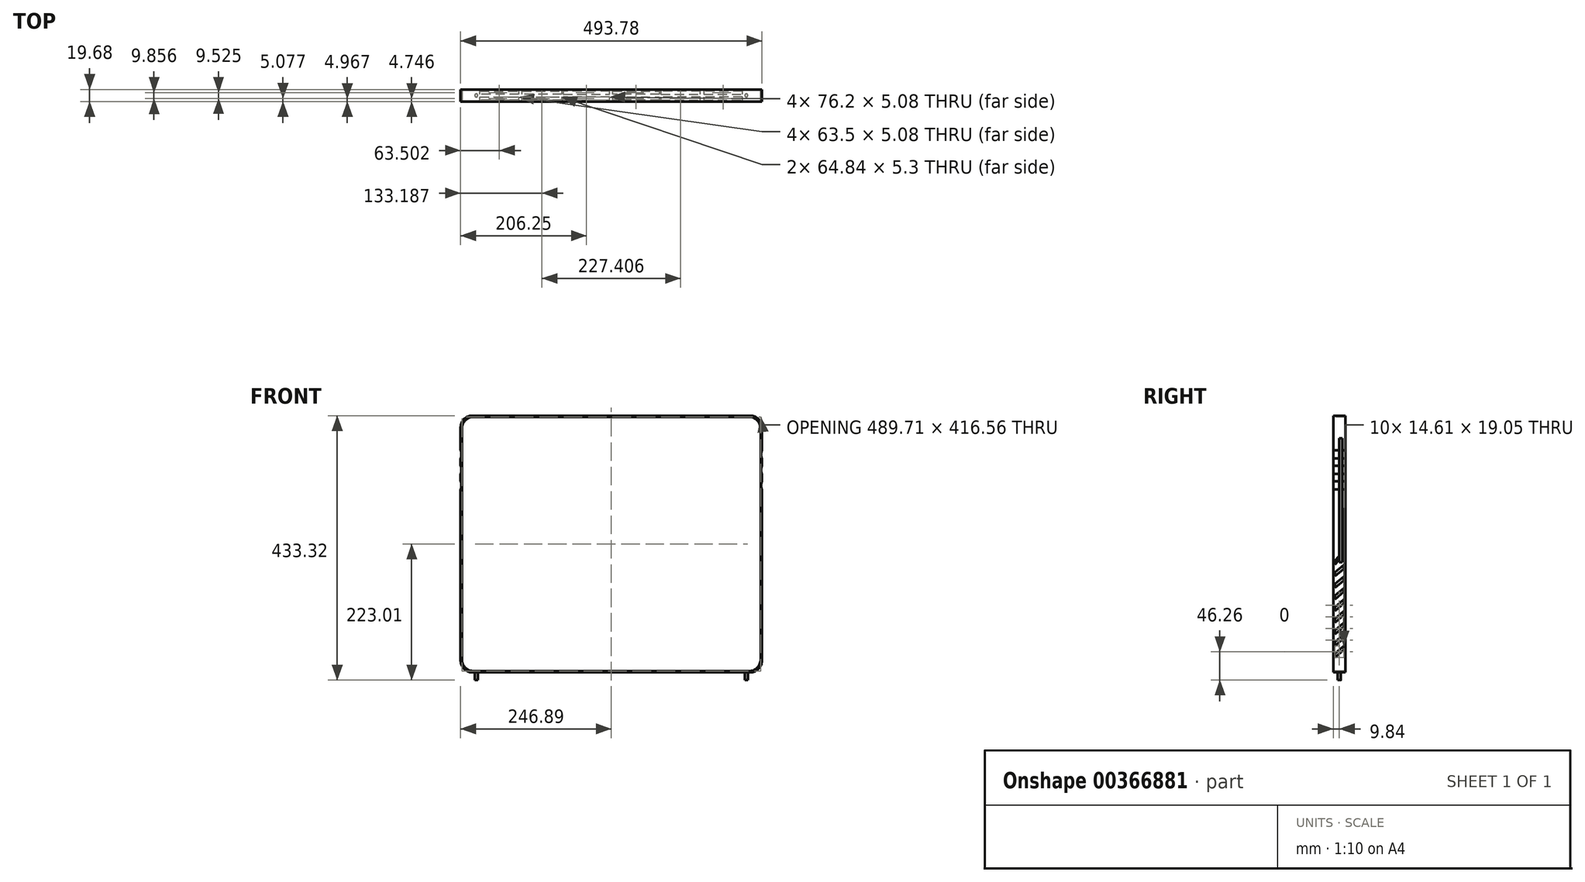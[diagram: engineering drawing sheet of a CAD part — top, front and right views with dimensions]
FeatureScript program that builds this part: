
annotation { "Feature Type Name" : "Feature", "Feature Type Description" : "" }
export const myFeature = defineFeature(function(context is Context, id is Id, definition is map)
    precondition{}
    {
        {
            var Q0;
            Q0=qCreatedBy(makeId("Front.planeOp"),FACE);
            var sketch = newSketch(context, id + "F0", { "sketchPlane" : qUnion([Q0])});
            skLineSegment(sketch, "E0.bottom", {"start": v(246.89, 210.31) * mm, "end": v(-246.89, 210.31) * mm});
            skLineSegment(sketch, "E0.top", {"start": v(246.89, -210.31) * mm, "end": v(-246.89, -210.31) * mm});
            skLineSegment(sketch, "E0.left", {"start": v(246.89, 210.31) * mm, "end": v(246.89, -210.31) * mm});
            skLineSegment(sketch, "E0.right", {"start": v(-246.89, 210.31) * mm, "end": v(-246.89, -210.31) * mm});
            skPoint(sketch, "E0.middle", {"position": v(0, 0) * mm});
            skSolve(sketch);
        }
        {
            var Q0;
            Q0 = qSketchRegion(id + "F0", true);
            extrude(context, id + "F1", {"entities" : qUnion([Q0]), "endBound" : BoundingType.SYMMETRIC, "oppositeDirection" : true, "depth" : 19.68 * mm});
        }
        {
            var Q0;
            Q0=makeQuery(id+"F1.opExtrude","SWEPT_EDGE",EDGE,{"disambiguationData":[OSD([sQuery(id+"F0.wireOp",EDGE,"E0.bottom"),sQuery(id+"F0.wireOp",EDGE,"E0.left")])]});
            fillet(context, id + "F2", {"entities" : qUnion([Q0]), "radius" : 19.05 * mm, "tangentPropagation" : true, "allowEdgeOverflow" : false});
        }
        {
            var Q0;
            Q0=makeQuery(id+"F1.opExtrude","SWEPT_EDGE",EDGE,{"disambiguationData":[OSD([sQuery(id+"F0.wireOp",EDGE,"E0.bottom"),sQuery(id+"F0.wireOp",EDGE,"E0.right")])]});
            fillet(context, id + "F3", {"entities" : qUnion([Q0]), "radius" : 19.05 * mm, "tangentPropagation" : true, "allowEdgeOverflow" : false});
        }
        {
            var Q0;
            Q0=makeQuery(id+"F1.opExtrude","SWEPT_EDGE",EDGE,{"disambiguationData":[OSD([sQuery(id+"F0.wireOp",EDGE,"E0.top"),sQuery(id+"F0.wireOp",EDGE,"E0.left")])]});
            fillet(context, id + "F4", {"entities" : qUnion([Q0]), "radius" : 19.05 * mm, "tangentPropagation" : true, "allowEdgeOverflow" : false});
        }
        {
            var Q0;
            Q0=makeQuery(id+"F1.opExtrude","SWEPT_EDGE",EDGE,{"disambiguationData":[OSD([sQuery(id+"F0.wireOp",EDGE,"E0.top"),sQuery(id+"F0.wireOp",EDGE,"E0.right")])]});
            fillet(context, id + "F5", {"entities" : qUnion([Q0]), "radius" : 19.05 * mm, "tangentPropagation" : true, "allowEdgeOverflow" : false});
        }
        {
            var Q0;
            Q0=qCreatedBy(makeId("Front.planeOp"),FACE);
            var sketch = newSketch(context, id + "F6", { "sketchPlane" : qUnion([Q0])});
            skLineSegment(sketch, "E1.bottom", {"start": v(225.8, 208.28) * mm, "end": v(-225.8, 208.28) * mm});
            skLineSegment(sketch, "E1.top", {"start": v(225.8, -208.28) * mm, "end": v(-225.8, -208.28) * mm});
            skLineSegment(sketch, "E1.left", {"start": v(244.86, 189.23) * mm, "end": v(244.86, -189.23) * mm});
            skLineSegment(sketch, "E1.right", {"start": v(-244.86, 189.23) * mm, "end": v(-244.86, -189.23) * mm});
            skPoint(sketch, "E1.middle", {"position": v(0, 0) * mm});
            skPoint(sketch, "E2.visualSharp", {"position": v(-244.86, 208.28) * mm});
            skArc(sketch, "E2.filletArc", {"start": v(-225.8, 208.28) * mm, "mid": v(-239.28, 202.7) * mm, "end": v(-244.86, 189.23) * mm});
            skPoint(sketch, "E3.visualSharp", {"position": v(244.86, 208.28) * mm});
            skArc(sketch, "E3.filletArc", {"start": v(244.86, 189.23) * mm, "mid": v(239.28, 202.7) * mm, "end": v(225.8, 208.28) * mm});
            skPoint(sketch, "E4.visualSharp", {"position": v(-244.86, -208.28) * mm});
            skArc(sketch, "E4.filletArc", {"start": v(-244.86, -189.23) * mm, "mid": v(-239.28, -202.7) * mm, "end": v(-225.8, -208.28) * mm});
            skPoint(sketch, "E5.visualSharp", {"position": v(244.86, -208.28) * mm});
            skArc(sketch, "E5.filletArc", {"start": v(225.8, -208.28) * mm, "mid": v(239.28, -202.7) * mm, "end": v(244.86, -189.23) * mm});
            skSolve(sketch);
        }
        {
            var Q0;
            Q0 = qSketchRegion(id + "F6", true);
            var Q1;
            Q1=sQuery(id+"F6.wireOp",EDGE,"E2.filletArc");
            var Q2;
            Q2=sQuery(id+"F6.wireOp",EDGE,"E1.bottom");
            var Q3;
            Q3=sQuery(id+"F6.wireOp",EDGE,"E3.filletArc");
            var Q4;
            Q4=sQuery(id+"F6.wireOp",EDGE,"E1.left");
            var Q5;
            Q5=sQuery(id+"F6.wireOp",EDGE,"E5.filletArc");
            var Q6;
            Q6=sQuery(id+"F6.wireOp",EDGE,"E1.top");
            var Q7;
            Q7=sQuery(id+"F6.wireOp",EDGE,"E4.filletArc");
            var Q8;
            Q8=sQuery(id+"F6.wireOp",EDGE,"E1.right");
            extrude(context, id + "F7", {"entities" : qUnion([Q0]), "operationType" : NewBodyOperationType.REMOVE, "surfaceEntities" : qUnion([Q1, Q2, Q3, Q4, Q5, Q6, Q7, Q8]), "endBound" : BoundingType.THROUGH_ALL, "oppositeDirection" : true, "depth" : 25.4 * mm});
        }
        {
            var Q0;
            Q0 = qSketchRegion(id + "F6", true);
            extrude(context, id + "F8", {"entities" : qUnion([Q0]), "operationType" : NewBodyOperationType.REMOVE, "oppositeDirection" : true, "depth" : 50.8 * mm});
        }
        {
            var Q0;
            Q0 = qSketchRegion(id + "F6", true);
            extrude(context, id + "F9", {"entities" : qUnion([Q0]), "operationType" : NewBodyOperationType.REMOVE, "endBound" : BoundingType.THROUGH_ALL, "depth" : 76.2 * mm});
        }
        {
            var Q0;
            Q0=qCreatedBy(makeId("Right.planeOp"),FACE);
            var sketch = newSketch(context, id + "F10", { "sketchPlane" : qUnion([Q0])});
            skLineSegment(sketch, "E6", {"start": v(7.3, -34.52) * mm, "end": v(7.3, -40.87) * mm});
            skLineSegment(sketch, "E7", {"start": v(7.3, -53.57) * mm, "end": v(7.3, -59.92) * mm});
            skLineSegment(sketch, "E8", {"start": v(-7.3, -46.58) * mm, "end": v(-7.3, -52.92) * mm});
            skLineSegment(sketch, "E9", {"start": v(-7.3, -52.92) * mm, "end": v(7.3, -40.87) * mm});
            skLineSegment(sketch, "E10", {"start": v(7.3, -34.52) * mm, "end": v(-7.3, -46.58) * mm});
            skLineSegment(sketch, "E11", {"start": v(-7.3, -65.62) * mm, "end": v(-7.3, -71.97) * mm});
            skLineSegment(sketch, "E12", {"start": v(-7.3, -65.62) * mm, "end": v(7.3, -53.57) * mm});
            skLineSegment(sketch, "E13", {"start": v(7.3, -59.92) * mm, "end": v(-7.3, -71.97) * mm});
            skLineSegment(sketch, "E14", {"start": v(-7.3, -33.88) * mm, "end": v(-7.3, -27.54) * mm});
            skLineSegment(sketch, "E15", {"start": v(-7.3, -33.88) * mm, "end": v(-1.32, -27.53) * mm});
            skLineSegment(sketch, "E16", {"start": v(-1.32, -27.53) * mm, "end": v(-1.32, -21.17) * mm});
            skLineSegment(sketch, "E17", {"start": v(-7.3, -27.54) * mm, "end": v(-1.32, -21.17) * mm});
            skLineSegment(sketch, "E18", {"start": v(-7.3, -84.67) * mm, "end": v(-7.3, -91.02) * mm});
            skLineSegment(sketch, "E19", {"start": v(7.3, -72.62) * mm, "end": v(7.3, -78.32) * mm});
            skLineSegment(sketch, "E20", {"start": v(-7.3, -84.67) * mm, "end": v(7.3, -72.62) * mm});
            skLineSegment(sketch, "E21", {"start": v(7.3, -78.32) * mm, "end": v(-7.3, -91.02) * mm});
            skLineSegment(sketch, "E22", {"start": v(-7.3, -103.72) * mm, "end": v(-7.3, -110.07) * mm});
            skLineSegment(sketch, "E23", {"start": v(7.3, -97.37) * mm, "end": v(7.3, -91.02) * mm});
            skLineSegment(sketch, "E24", {"start": v(-7.3, -103.72) * mm, "end": v(7.3, -91.02) * mm});
            skLineSegment(sketch, "E25", {"start": v(7.3, -97.37) * mm, "end": v(-7.3, -110.07) * mm});
            skLineSegment(sketch, "E26", {"start": v(-7.3, -122.77) * mm, "end": v(-7.3, -129.12) * mm});
            skLineSegment(sketch, "E27", {"start": v(-7.3, -129.12) * mm, "end": v(7.3, -116.42) * mm});
            skLineSegment(sketch, "E28", {"start": v(7.3, -116.42) * mm, "end": v(7.3, -110.07) * mm});
            skLineSegment(sketch, "E29", {"start": v(7.3, -110.07) * mm, "end": v(-7.3, -122.77) * mm});
            skLineSegment(sketch, "E30", {"start": v(-7.3, -141.82) * mm, "end": v(-7.3, -148.17) * mm});
            skLineSegment(sketch, "E31", {"start": v(-7.3, -148.17) * mm, "end": v(7.3, -135.47) * mm});
            skLineSegment(sketch, "E32", {"start": v(7.3, -135.47) * mm, "end": v(7.3, -129.12) * mm});
            skLineSegment(sketch, "E33", {"start": v(7.3, -129.12) * mm, "end": v(-7.3, -141.82) * mm});
            skLineSegment(sketch, "E34", {"start": v(-7.3, -160.87) * mm, "end": v(-7.3, -167.22) * mm});
            skLineSegment(sketch, "E35", {"start": v(-7.3, -167.22) * mm, "end": v(7.3, -154.52) * mm});
            skLineSegment(sketch, "E36", {"start": v(7.3, -154.52) * mm, "end": v(7.3, -148.17) * mm});
            skLineSegment(sketch, "E37", {"start": v(7.3, -148.17) * mm, "end": v(-7.3, -160.87) * mm});
            skLineSegment(sketch, "E38", {"start": v(-7.3, -179.92) * mm, "end": v(-7.3, -186.27) * mm});
            skLineSegment(sketch, "E39", {"start": v(-7.3, -186.27) * mm, "end": v(7.3, -173.57) * mm});
            skLineSegment(sketch, "E40", {"start": v(7.3, -173.57) * mm, "end": v(7.3, -167.22) * mm});
            skLineSegment(sketch, "E41", {"start": v(7.3, -167.22) * mm, "end": v(-7.3, -179.92) * mm});
            skSolve(sketch);
        }
        {
            var Q0;
            Q0 = qSketchRegion(id + "F10", true);
            extrude(context, id + "F11", {"entities" : qUnion([Q0]), "operationType" : NewBodyOperationType.REMOVE, "oppositeDirection" : true, "depth" : 381 * mm});
        }
        {
            var Q0;
            Q0 = qSketchRegion(id + "F10", true);
            extrude(context, id + "F12", {"entities" : qUnion([Q0]), "operationType" : NewBodyOperationType.REMOVE, "depth" : 381 * mm});
        }
        {
            var Q0;
            Q0=qCreatedBy(makeId("Top.planeOp"),FACE);
            var sketch = newSketch(context, id + "F13", { "sketchPlane" : qUnion([Q0])});
            skLineSegment(sketch, "E42", {"start": v(-2.54, -7.3) * mm, "end": v(-2.54, -2.22) * mm});
            skLineSegment(sketch, "E43", {"start": v(-2.54, -2.22) * mm, "end": v(-78.74, -2.22) * mm});
            skLineSegment(sketch, "E44", {"start": v(-78.74, -2.22) * mm, "end": v(-78.74, -7.3) * mm});
            skLineSegment(sketch, "E45", {"start": v(-78.74, -7.3) * mm, "end": v(-2.54, -7.3) * mm});
            skLineSegment(sketch, "E46", {"start": v(-78.74, 2.22) * mm, "end": v(-2.54, 2.22) * mm});
            skLineSegment(sketch, "E47", {"start": v(-2.54, 2.22) * mm, "end": v(-2.54, 7.3) * mm});
            skLineSegment(sketch, "E48", {"start": v(-2.54, 7.3) * mm, "end": v(-78.74, 7.3) * mm});
            skLineSegment(sketch, "E49", {"start": v(-78.74, 7.3) * mm, "end": v(-78.74, 2.22) * mm});
            skLineSegment(sketch, "E50", {"start": v(-215.14, -7.63) * mm, "end": v(-215.14, -2.55) * mm});
            skLineSegment(sketch, "E51", {"start": v(-215.14, -2.55) * mm, "end": v(-151.64, -2.55) * mm});
            skLineSegment(sketch, "E52", {"start": v(-151.64, -2.55) * mm, "end": v(-151.64, -7.52) * mm});
            skLineSegment(sketch, "E53", {"start": v(-151.64, -7.52) * mm, "end": v(-215.14, -7.63) * mm});
            skLineSegment(sketch, "E54", {"start": v(-215.14, 2.22) * mm, "end": v(-215.14, 7.3) * mm});
            skLineSegment(sketch, "E55", {"start": v(-215.14, 7.3) * mm, "end": v(-151.64, 7.3) * mm});
            skLineSegment(sketch, "E56", {"start": v(-151.64, 7.3) * mm, "end": v(-151.64, 2.22) * mm});
            skLineSegment(sketch, "E57", {"start": v(-151.64, 2.22) * mm, "end": v(-215.14, 2.22) * mm});
            skLineSegment(sketch, "E58", {"start": v(-146.13, -7.52) * mm, "end": v(-146.13, -2.55) * mm});
            skLineSegment(sketch, "E59", {"start": v(-146.13, -2.55) * mm, "end": v(-81.3, -2.22) * mm});
            skLineSegment(sketch, "E60", {"start": v(-81.3, -2.22) * mm, "end": v(-81.28, -7.52) * mm});
            skLineSegment(sketch, "E61", {"start": v(-81.28, -7.52) * mm, "end": v(-146.13, -7.52) * mm});
            skLineSegment(sketch, "E62", {"start": v(-146.13, 2.22) * mm, "end": v(-146.13, 7.3) * mm});
            skLineSegment(sketch, "E63", {"start": v(-146.13, 7.3) * mm, "end": v(-81.3, 7.3) * mm});
            skLineSegment(sketch, "E64", {"start": v(-81.3, 7.3) * mm, "end": v(-81.3, 2.22) * mm});
            skLineSegment(sketch, "E65", {"start": v(-81.3, 2.22) * mm, "end": v(-146.13, 2.22) * mm});
            skLineSegment(sketch, "E66.MirrorCS", {"start": v(78.74, -7.3) * mm, "end": v(2.54, -7.3) * mm});
            skLineSegment(sketch, "E67.MirrorCS", {"start": v(2.54, -2.22) * mm, "end": v(78.74, -2.22) * mm});
            skLineSegment(sketch, "E68.MirrorCS", {"start": v(78.74, 2.22) * mm, "end": v(2.54, 2.22) * mm});
            skLineSegment(sketch, "E69.MirrorCS", {"start": v(2.54, 7.3) * mm, "end": v(78.74, 7.3) * mm});
            skLineSegment(sketch, "E70.MirrorCS", {"start": v(81.28, -7.52) * mm, "end": v(146.13, -7.52) * mm});
            skLineSegment(sketch, "E71.MirrorCS", {"start": v(146.13, -2.55) * mm, "end": v(81.3, -2.22) * mm});
            skLineSegment(sketch, "E72.MirrorCS", {"start": v(81.3, 2.22) * mm, "end": v(146.13, 2.22) * mm});
            skLineSegment(sketch, "E73.MirrorCS", {"start": v(146.13, 7.3) * mm, "end": v(81.3, 7.3) * mm});
            skLineSegment(sketch, "E74.MirrorCS", {"start": v(151.64, -7.52) * mm, "end": v(215.14, -7.63) * mm});
            skLineSegment(sketch, "E75.MirrorCS", {"start": v(215.14, -2.55) * mm, "end": v(151.64, -2.55) * mm});
            skLineSegment(sketch, "E76.MirrorCS", {"start": v(151.64, 2.22) * mm, "end": v(215.14, 2.22) * mm});
            skLineSegment(sketch, "E77.MirrorCS", {"start": v(215.14, 7.3) * mm, "end": v(151.64, 7.3) * mm});
            skLineSegment(sketch, "E78.MirrorCS", {"start": v(215.14, -7.63) * mm, "end": v(215.14, -2.55) * mm});
            skLineSegment(sketch, "E79.MirrorCS", {"start": v(151.64, -2.55) * mm, "end": v(151.64, -7.52) * mm});
            skLineSegment(sketch, "E80.MirrorCS", {"start": v(146.13, -7.52) * mm, "end": v(146.13, -2.55) * mm});
            skLineSegment(sketch, "E81.MirrorCS", {"start": v(151.64, 7.3) * mm, "end": v(151.64, 2.22) * mm});
            skLineSegment(sketch, "E82.MirrorCS", {"start": v(81.3, 7.3) * mm, "end": v(81.3, 2.22) * mm});
            skLineSegment(sketch, "E83.MirrorCS", {"start": v(2.54, -7.3) * mm, "end": v(2.54, -2.22) * mm});
            skLineSegment(sketch, "E84.MirrorCS", {"start": v(2.54, 2.22) * mm, "end": v(2.54, 7.3) * mm});
            skLineSegment(sketch, "E85.MirrorCS", {"start": v(78.74, -2.22) * mm, "end": v(78.74, -7.3) * mm});
            skLineSegment(sketch, "E86.MirrorCS", {"start": v(78.74, 7.3) * mm, "end": v(78.74, 2.22) * mm});
            skLineSegment(sketch, "E87.MirrorCS", {"start": v(215.14, 2.22) * mm, "end": v(215.14, 7.3) * mm});
            skLineSegment(sketch, "E88.MirrorCS", {"start": v(146.13, 2.22) * mm, "end": v(146.13, 7.3) * mm});
            skLineSegment(sketch, "E89", {"start": v(81.3, -2.22) * mm, "end": v(81.28, -7.52) * mm});
            skSolve(sketch);
        }
        {
            var Q0;
            Q0 = qSketchRegion(id + "F13", true);
            extrude(context, id + "F14", {"entities" : qUnion([Q0]), "operationType" : NewBodyOperationType.REMOVE, "oppositeDirection" : true, "depth" : 254 * mm});
        }
        {
            var Q0;
            Q0=qCreatedBy(makeId("Front.planeOp"),FACE);
            var sketch = newSketch(context, id + "F15", { "sketchPlane" : qUnion([Q0])});
            skCircle(sketch, "E90", {"center": v(-264.67, 146.81) * mm, "radius": 19.05 * mm});
            skCircle(sketch, "E91", {"center": v(-264.67, 121.41) * mm, "radius": 19.05 * mm});
            skCircle(sketch, "E92", {"center": v(-264.67, 96.01) * mm, "radius": 19.05 * mm});
            skCircle(sketch, "E93.MirrorC", {"center": v(264.67, 96.01) * mm, "radius": 19.05 * mm});
            skCircle(sketch, "E94.MirrorC", {"center": v(264.67, 121.41) * mm, "radius": 19.05 * mm});
            skCircle(sketch, "E95.MirrorC", {"center": v(264.67, 146.81) * mm, "radius": 19.05 * mm});
            skSolve(sketch);
        }
        {
            var Q0;
            Q0 = qSketchRegion(id + "F15", true);
            extrude(context, id + "F16", {"entities" : qUnion([Q0]), "operationType" : NewBodyOperationType.REMOVE, "endBound" : BoundingType.SYMMETRIC, "depth" : 127 * mm});
        }
        {
            var Q0;
            Q0=qCreatedBy(makeId("Top.planeOp"),FACE);
            var sketch = newSketch(context, id + "F17", { "sketchPlane" : qUnion([Q0])});
            skCircle(sketch, "E96", {"center": v(-221.3, 0) * mm, "radius": 2.48 * mm});
            skCircle(sketch, "E97.MirrorC", {"center": v(221.3, 0) * mm, "radius": 2.48 * mm});
            skSolve(sketch);
        }
        {
            var Q0;
            Q0 = qSketchRegion(id + "F17", true);
            extrude(context, id + "F18", {"entities" : qUnion([Q0]), "operationType" : NewBodyOperationType.ADD, "oppositeDirection" : true, "depth" : 223 * mm});
        }
        {
            var Q0;
            Q0 = qSketchRegion(id + "F17", true);
            extrude(context, id + "F19", {"entities" : qUnion([Q0]), "operationType" : NewBodyOperationType.REMOVE, "oppositeDirection" : true, "depth" : 208.28 * mm});
        }
        {
            var Q0;
            Q0=qCreatedBy(makeId("Right.planeOp"),FACE);
            var sketch = newSketch(context, id + "F20", { "sketchPlane" : qUnion([Q0])});
            skLineSegment(sketch, "E98.bottom", {"start": v(0, -29.95) * mm, "end": v(5.08, -29.95) * mm});
            skLineSegment(sketch, "E98.top", {"start": v(0, 173.25) * mm, "end": v(5.08, 173.25) * mm});
            skLineSegment(sketch, "E98.left", {"start": v(0, -29.95) * mm, "end": v(0, 173.25) * mm});
            skLineSegment(sketch, "E98.right", {"start": v(5.08, -29.95) * mm, "end": v(5.08, 173.25) * mm});
            skSolve(sketch);
        }
        {
            var Q0;
            Q0 = qSketchRegion(id + "F20", true);
            extrude(context, id + "F21", {"entities" : qUnion([Q0]), "operationType" : NewBodyOperationType.REMOVE, "depth" : 254 * mm});
        }
    });
